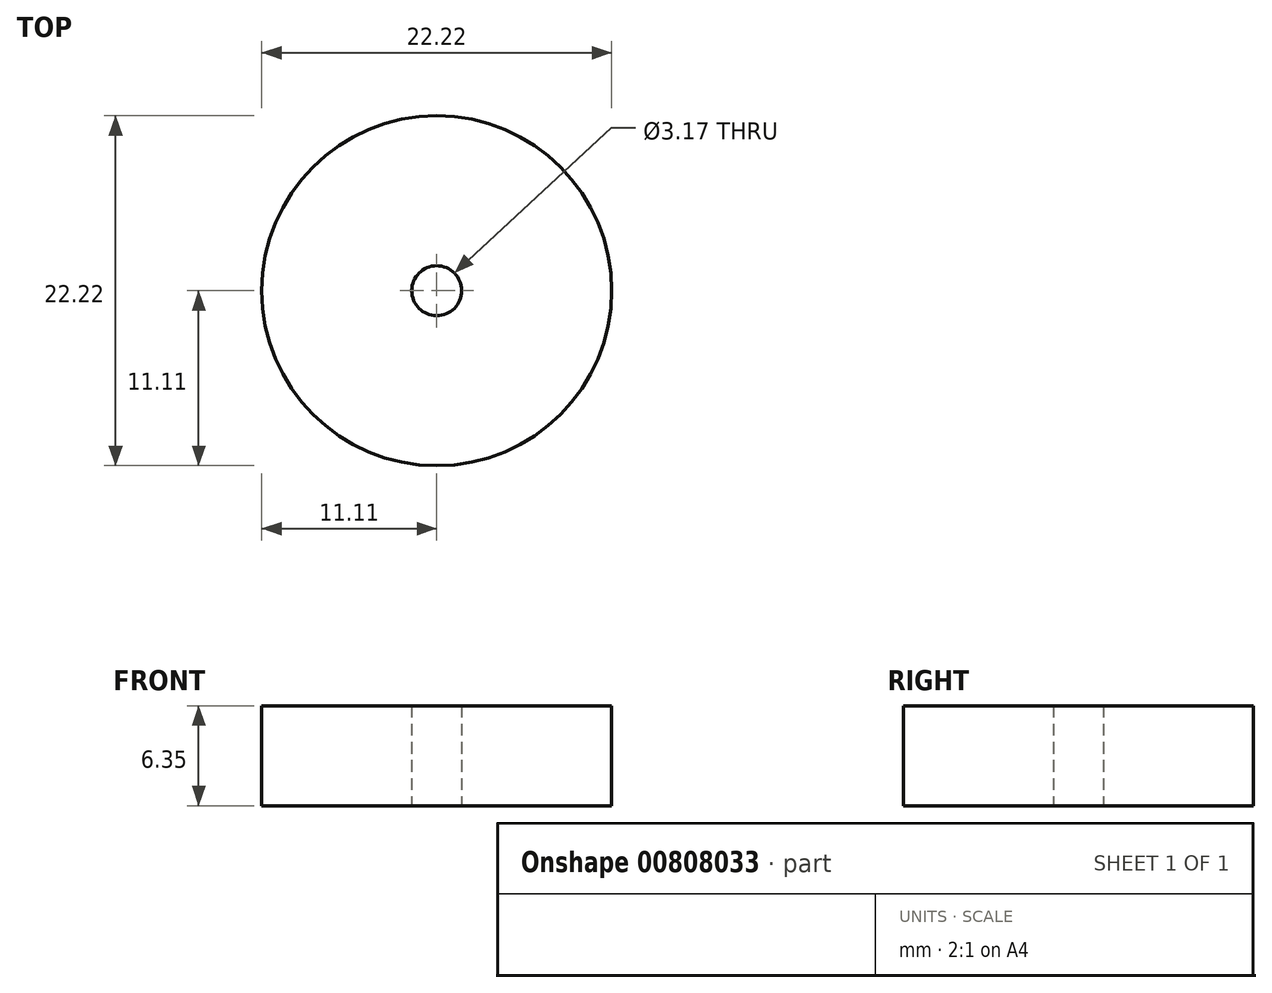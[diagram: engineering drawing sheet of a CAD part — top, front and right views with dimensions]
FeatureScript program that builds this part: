
annotation { "Feature Type Name" : "Feature", "Feature Type Description" : "" }
export const myFeature = defineFeature(function(context is Context, id is Id, definition is map)
    precondition{}
    {
        {
            var Q0;
            Q0=qCreatedBy(makeId("Top.planeOp"),FACE);
            var sketch = newSketch(context, id + "F0", { "sketchPlane" : qUnion([Q0])});
            skCircle(sketch, "E0", {"center": v(0, 0) * mm, "radius": 11.11 * mm});
            skCircle(sketch, "E1", {"center": v(0, 0) * mm, "radius": 1.59 * mm});
            skSolve(sketch);
        }
        {
            var Q0;
            Q0 = qSketchRegion(id + "F0", true);
            extrude(context, id + "F1", {"entities" : qUnion([Q0]), "depth" : 6.35 * mm, "offsetDistance" : 25.4 * mm});
        }
    });
